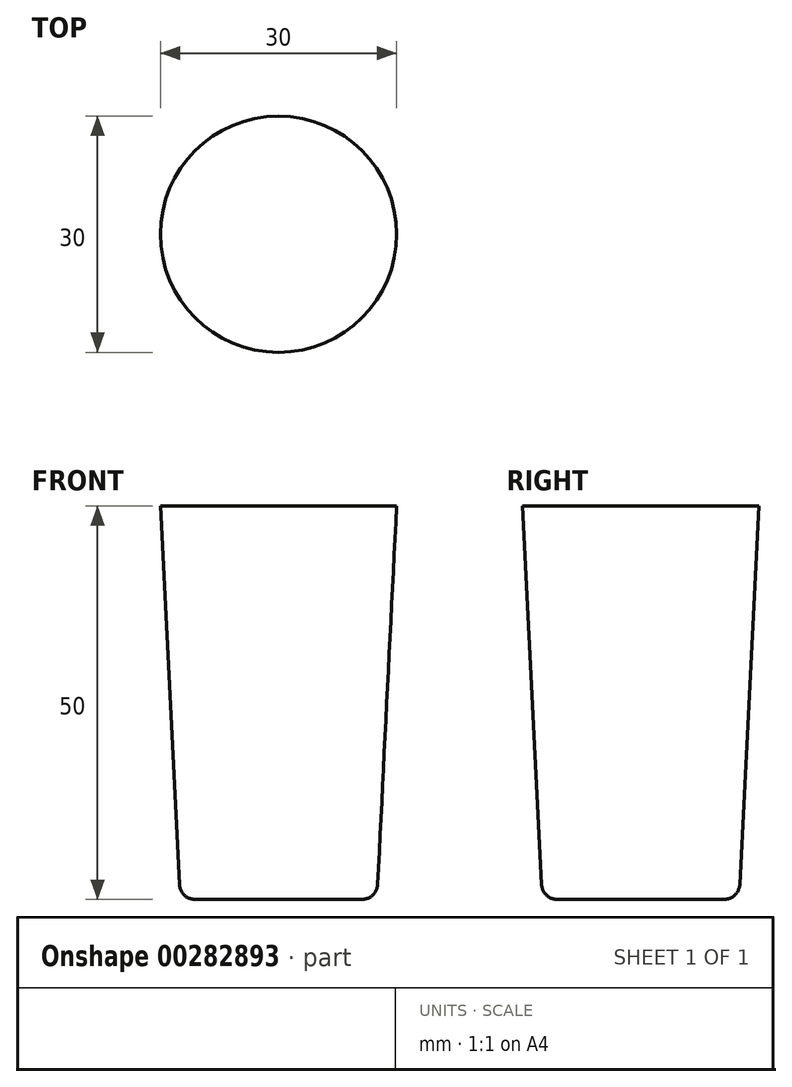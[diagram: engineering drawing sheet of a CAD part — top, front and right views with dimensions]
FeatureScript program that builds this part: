
annotation { "Feature Type Name" : "Feature", "Feature Type Description" : "" }
export const myFeature = defineFeature(function(context is Context, id is Id, definition is map)
    precondition{}
    {
        {
            var Q0;
            Q0=qCreatedBy(makeId("Front.planeOp"),FACE);
            var sketch = newSketch(context, id + "F0", { "sketchPlane" : qUnion([Q0])});
            skLineSegment(sketch, "E0", {"start": v(0, 0) * mm, "end": v(0, -99.56) * mm, "construction": true});
            skLineSegment(sketch, "E1", {"start": v(-15, 0) * mm, "end": v(-12.5, -50) * mm});
            skLineSegment(sketch, "E2", {"start": v(-12.5, -50) * mm, "end": v(0, -50) * mm});
            skLineSegment(sketch, "E3", {"start": v(0, -50) * mm, "end": v(0, 0) * mm});
            skLineSegment(sketch, "E4", {"start": v(-15, 0) * mm, "end": v(0, 0) * mm});
            skSolve(sketch);
        }
        {
            var Q0;
            Q0 = qSketchRegion(id + "F0", true);
            var Q1;
            Q1=sQuery(id+"F0.wireOp",EDGE,"E0");
            revolve(context, id + "F1", {"entities" : qUnion([Q0]), "axis" : qUnion([Q1]), "revolveType" : RevolveType.FULL});
        }
        {
            var Q0;
            Q0=makeQuery(id+"F1.opRevolve","SWEPT_EDGE",EDGE,{"disambiguationData":[OSD([sQuery(id+"F0.wireOp",EDGE,"E1"),sQuery(id+"F0.wireOp",EDGE,"E2")])]});
            fillet(context, id + "F2", {"entities" : qUnion([Q0]), "radius" : 2 * mm, "tangentPropagation" : true, "allowEdgeOverflow" : false});
        }
    });
